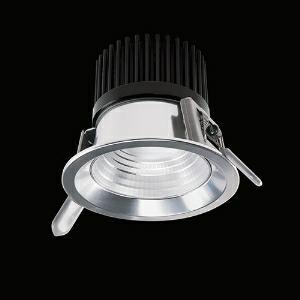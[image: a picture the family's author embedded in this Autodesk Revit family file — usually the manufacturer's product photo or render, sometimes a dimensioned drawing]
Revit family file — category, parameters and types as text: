
# Revit family: spectral_myral_myral_1500-840-m
name_source: partatom
category: Lighting Fixtures
revit_build: Autodesk Revit 2016 (Build: 20150220_1215(x64)
units: mm (PartAtom-declared; Revit-internal decimal feet)

## family parameters
Cut with Voids When Loaded = No
Host = Face
Light Source = No
Part Type = Normal
Room Calculation Point = No
Round Connector Dimension = Use Diameter
Shared = No

## types (1)
- SPECTRAL MYRAL (1 x )
    Apparent Load = 0 VA
    Approval mark = CE
    CIE Flux Codes = 82 99 100 100 100
    Control Gear = Electronic transformer
    Default Elevation = 1800 mm
    Description = SPG0320179
MYRAL recessed spot

Design:
    Height = 0 mm  [stored 0 ft]
    Lamp = 1 x
    Lamp count = 1
    Length = 120 mm
    Luminous efficacy = 0 lm/W
    Manufacturer = Ridi
    ModVariant = No
    Model = MYRAL 1500-840-M
    Mounting Place = Ceiling
    Mounting Type = Recessed
    Number of Poles = 1
    OnlyDefault = Yes
    Power Factor = 1
    Product Name = SPECTRAL MYRAL
    Product group = Downlight recessed
    ProductGroupID = 400
    Protection Class = Protection class
    Protection Degree = IP 20
    RlxData = <blob elided: 38653 chars, md5=0979d4bb>
    Socket = socket
    Standby Power = 0 W
    System Light Flux = 0 lm
    System Power = 0 W
    Type Image = myral_04.jpg
    URL = http://reluxnet.relux.com
    VarID = ---
    Voltage = 0 V
    Weight = 0.00 kg
    Width = 0 mm  [stored 0 ft]

note: [stored X ft] marks values corroborated as IEEE doubles in the binary element streams (Revit-internal decimal feet)

## geometry (parser evidence)
native form markers: Sweep x10
no freeform markers — native parametric forms only
